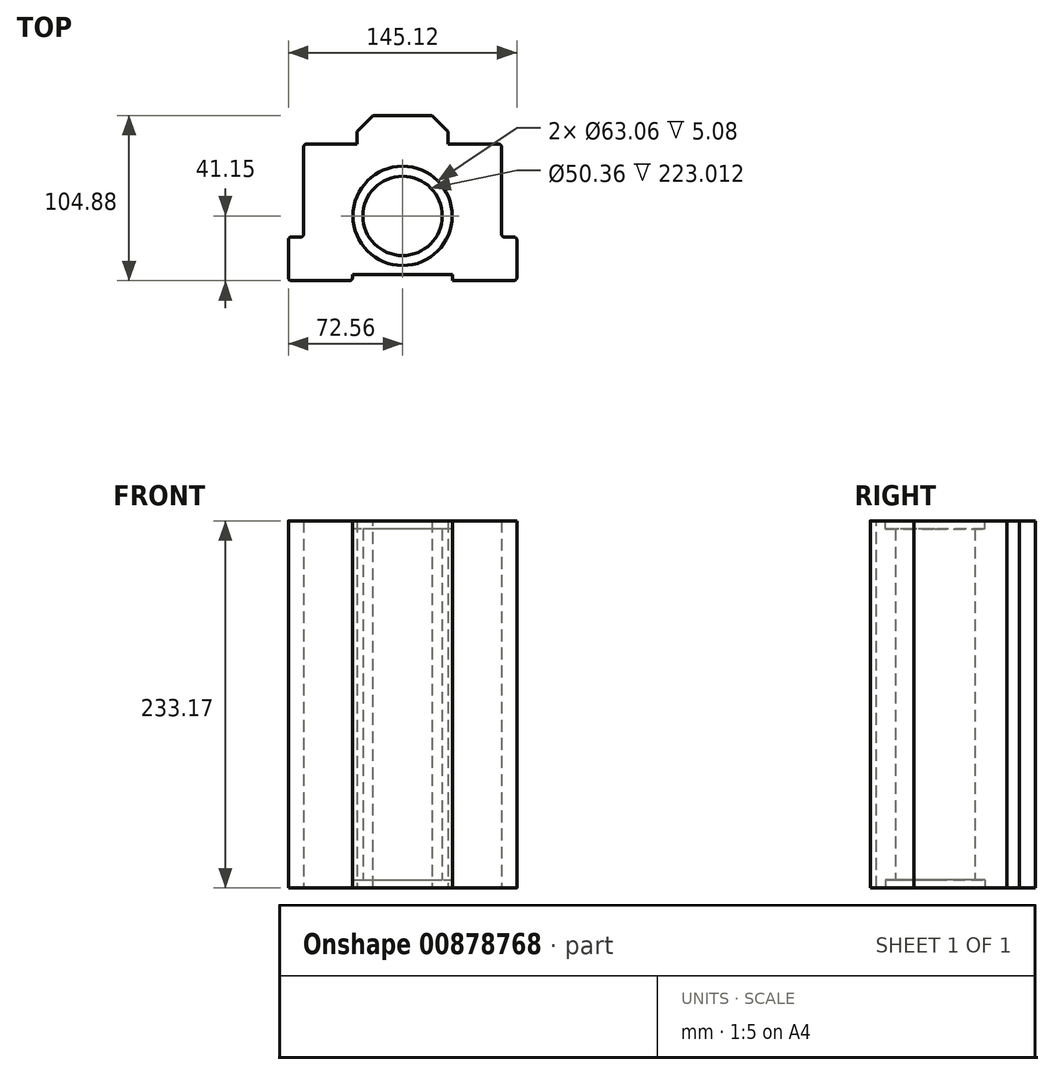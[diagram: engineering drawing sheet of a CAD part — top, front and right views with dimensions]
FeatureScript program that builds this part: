
annotation { "Feature Type Name" : "Feature", "Feature Type Description" : "" }
export const myFeature = defineFeature(function(context is Context, id is Id, definition is map)
    precondition{}
    {
        {
            var Q0;
            Q0=qCreatedBy(makeId("Top.planeOp"),FACE);
            var sketch = newSketch(context, id + "F0", { "sketchPlane" : qUnion([Q0])});
            skLineSegment(sketch, "E0.bottom", {"start": v(-62.86, 45.65) * mm, "end": v(-29, 45.65) * mm});
            skLineSegment(sketch, "E0.top", {"start": v(-62.86, -41.15) * mm, "end": v(62.86, -41.15) * mm});
            skLineSegment(sketch, "E0.left", {"start": v(-62.86, 45.65) * mm, "end": v(-62.86, -41.15) * mm});
            skLineSegment(sketch, "E0.right", {"start": v(62.86, 45.65) * mm, "end": v(62.86, -41.15) * mm});
            skCircle(sketch, "E1", {"center": v(0, 0) * mm, "radius": 25.18 * mm});
            skLineSegment(sketch, "E2.top", {"start": v(-29, 63.73) * mm, "end": v(29, 63.73) * mm});
            skLineSegment(sketch, "E2.left", {"start": v(-29, 45.65) * mm, "end": v(-29, 63.73) * mm});
            skLineSegment(sketch, "E2.right", {"start": v(29, 45.65) * mm, "end": v(29, 63.73) * mm});
            skLineSegment(sketch, "E3", {"start": v(0, 45.65) * mm, "end": v(0, -41.15) * mm, "construction": true});
            skLineSegment(sketch, "E4.trimOffspring", {"start": v(29, 45.65) * mm, "end": v(62.86, 45.65) * mm});
            skLineSegment(sketch, "E5", {"start": v(-29, 45.65) * mm, "end": v(0, 45.65) * mm});
            skLineSegment(sketch, "E6", {"start": v(29, 45.65) * mm, "end": v(0, 45.65) * mm});
            skLineSegment(sketch, "E7.bottom", {"start": v(-62.86, -41.15) * mm, "end": v(-72.56, -41.15) * mm});
            skLineSegment(sketch, "E7.top", {"start": v(-62.86, -13.43) * mm, "end": v(-72.56, -13.43) * mm});
            skLineSegment(sketch, "E7.left", {"start": v(-62.86, -41.15) * mm, "end": v(-62.86, -13.43) * mm});
            skLineSegment(sketch, "E7.right", {"start": v(-72.56, -41.15) * mm, "end": v(-72.56, -13.43) * mm});
            skLineSegment(sketch, "E8.bottom", {"start": v(62.86, -41.15) * mm, "end": v(72.56, -41.15) * mm});
            skLineSegment(sketch, "E8.top", {"start": v(62.86, -13.43) * mm, "end": v(72.56, -13.43) * mm});
            skLineSegment(sketch, "E8.left", {"start": v(62.86, -41.15) * mm, "end": v(62.86, -13.43) * mm});
            skLineSegment(sketch, "E8.right", {"start": v(72.56, -41.15) * mm, "end": v(72.56, -13.43) * mm});
            skSolve(sketch);
        }
        {
            var Q0;
            Q0 = qSketchRegion(id + "F0", true);
            extrude(context, id + "F1", {"entities" : qUnion([Q0]), "depth" : 233.17 * mm, "offsetDistance" : 25.4 * mm});
        }
        {
            var Q0;
            Q0=makeQuery(id+"F1.opExtrude","CAP_FACE",FACE,{"disambiguationData":[OSD([sQuery(id+"F0.wireOp",EDGE,"E0.bottom"),sQuery(id+"F0.wireOp",EDGE,"E0.top"),sQuery(id+"F0.wireOp",EDGE,"E0.left"),sQuery(id+"F0.wireOp",EDGE,"E0.right"),sQuery(id+"F0.wireOp",EDGE,"E1"),sQuery(id+"F0.wireOp",EDGE,"E2.top"),sQuery(id+"F0.wireOp",EDGE,"E2.left"),sQuery(id+"F0.wireOp",EDGE,"E2.right"),sQuery(id+"F0.wireOp",EDGE,"E4.trimOffspring"),sQuery(id+"F0.wireOp",EDGE,"E7.bottom"),sQuery(id+"F0.wireOp",EDGE,"E7.top"),sQuery(id+"F0.wireOp",EDGE,"E7.right"),sQuery(id+"F0.wireOp",EDGE,"E8.bottom"),sQuery(id+"F0.wireOp",EDGE,"E8.top"),sQuery(id+"F0.wireOp",EDGE,"E8.right")])],"isStart":false});
            var sketch = newSketch(context, id + "F2", { "sketchPlane" : qUnion([Q0])});
            skLineSegment(sketch, "E9.bottom", {"start": v(-31.8, -41.15) * mm, "end": v(31.8, -41.15) * mm});
            skLineSegment(sketch, "E9.top", {"start": v(-31.8, -37.14) * mm, "end": v(0, -37.14) * mm});
            skLineSegment(sketch, "E9.left", {"start": v(-31.8, -41.15) * mm, "end": v(-31.8, -37.14) * mm});
            skLineSegment(sketch, "E9.right", {"start": v(31.8, -41.15) * mm, "end": v(31.8, -37.14) * mm});
            skLineSegment(sketch, "E10", {"start": v(0, -41.15) * mm, "end": v(0, -37.14) * mm, "construction": true});
            skLineSegment(sketch, "E11", {"start": v(0, -37.14) * mm, "end": v(31.8, -37.14) * mm});
            skSolve(sketch);
        }
        {
            var Q0;
            Q0=makeQuery(id+"F2.imprint","IMPRINT",FACE,{"disambiguationData":[TD([[makeQuery(id+"F2.imprint","IMPRINT",EDGE,{"derivedFrom":sQuery(id+"F2.wireOp",EDGE,"E9.bottom")}),-1.0]])]});
            var Q1;
            Q1=makeQuery(id+"F1.opExtrude","CAP_FACE",FACE,{"disambiguationData":[OSD([sQuery(id+"F0.wireOp",EDGE,"E0.bottom"),sQuery(id+"F0.wireOp",EDGE,"E0.top"),sQuery(id+"F0.wireOp",EDGE,"E0.left"),sQuery(id+"F0.wireOp",EDGE,"E0.right"),sQuery(id+"F0.wireOp",EDGE,"E1"),sQuery(id+"F0.wireOp",EDGE,"E2.top"),sQuery(id+"F0.wireOp",EDGE,"E2.left"),sQuery(id+"F0.wireOp",EDGE,"E2.right"),sQuery(id+"F0.wireOp",EDGE,"E4.trimOffspring"),sQuery(id+"F0.wireOp",EDGE,"E7.bottom"),sQuery(id+"F0.wireOp",EDGE,"E7.top"),sQuery(id+"F0.wireOp",EDGE,"E7.right"),sQuery(id+"F0.wireOp",EDGE,"E8.bottom"),sQuery(id+"F0.wireOp",EDGE,"E8.top"),sQuery(id+"F0.wireOp",EDGE,"E8.right")])],"isStart":true});
            extrude(context, id + "F3", {"entities" : qUnion([Q0]), "operationType" : NewBodyOperationType.REMOVE, "endBound" : BoundingType.UP_TO_SURFACE, "oppositeDirection" : true, "depth" : 25.4 * mm, "endBoundEntityFace" : qUnion([Q1]), "offsetDistance" : 25.4 * mm});
        }
        {
            var Q0;
            Q0=makeQuery(id+"F1.opExtrude","SWEPT_EDGE",EDGE,{"disambiguationData":[OSD([sQuery(id+"F0.wireOp",EDGE,"E2.top"),sQuery(id+"F0.wireOp",EDGE,"E2.left")])]});
            var Q1;
            Q1=makeQuery(id+"F1.opExtrude","SWEPT_EDGE",EDGE,{"disambiguationData":[OSD([sQuery(id+"F0.wireOp",EDGE,"E2.top"),sQuery(id+"F0.wireOp",EDGE,"E2.right")])]});
            chamfer(context, id + "F4", {"entities" : qUnion([Q0, Q1]), "width" : 10.16 * mm, "tangentPropagation" : true});
        }
        {
            var Q0;
            Q0=makeQuery(id+"F1.opExtrude","SWEPT_EDGE",EDGE,{"disambiguationData":[OSD([sQuery(id+"F0.wireOp",EDGE,"E8.top"),sQuery(id+"F0.wireOp",EDGE,"E8.right")])]});
            var Q1;
            Q1=makeQuery(id+"F1.opExtrude","SWEPT_EDGE",EDGE,{"disambiguationData":[OSD([sQuery(id+"F0.wireOp",EDGE,"E8.bottom"),sQuery(id+"F0.wireOp",EDGE,"E8.right")])]});
            var Q2;
            Q2=makeQuery(id+"F3.boolean.opBoolean","COPY",EDGE,{"derivedFrom":makeQuery(id+"F3.opExtrude","SWEPT_EDGE",EDGE,{"disambiguationData":[OSD([sQuery(id+"F0.wireOp",EDGE,"E0.top"),sQuery(id+"F0.wireOp",EDGE,"E7.bottom"),sQuery(id+"F0.wireOp",EDGE,"E8.bottom"),sQuery(id+"F2.wireOp",EDGE,"E9.bottom"),sQuery(id+"F2.wireOp",EDGE,"E9.right")])]})});
            var Q3;
            Q3=makeQuery(id+"F3.boolean.opBoolean","COPY",EDGE,{"derivedFrom":makeQuery(id+"F3.opExtrude","SWEPT_EDGE",EDGE,{"disambiguationData":[OSD([sQuery(id+"F0.wireOp",EDGE,"E0.top"),sQuery(id+"F0.wireOp",EDGE,"E7.bottom"),sQuery(id+"F0.wireOp",EDGE,"E8.bottom"),sQuery(id+"F2.wireOp",EDGE,"E9.bottom"),sQuery(id+"F2.wireOp",EDGE,"E9.left")])]})});
            var Q4;
            Q4=makeQuery(id+"F1.opExtrude","SWEPT_EDGE",EDGE,{"disambiguationData":[OSD([sQuery(id+"F0.wireOp",EDGE,"E7.bottom"),sQuery(id+"F0.wireOp",EDGE,"E7.right")])]});
            var Q5;
            Q5=makeQuery(id+"F1.opExtrude","SWEPT_EDGE",EDGE,{"disambiguationData":[OSD([sQuery(id+"F0.wireOp",EDGE,"E7.top"),sQuery(id+"F0.wireOp",EDGE,"E7.right")])]});
            var Q6;
            Q6=makeQuery(id+"F1.opExtrude","SWEPT_EDGE",EDGE,{"disambiguationData":[OSD([sQuery(id+"F0.wireOp",EDGE,"E0.bottom"),sQuery(id+"F0.wireOp",EDGE,"E0.left")])]});
            var Q7;
            Q7=makeQuery(id+"F1.opExtrude","SWEPT_EDGE",EDGE,{"disambiguationData":[OSD([sQuery(id+"F0.wireOp",EDGE,"E0.right"),sQuery(id+"F0.wireOp",EDGE,"E4.trimOffspring")])]});
            var Q8;
            Q8=makeQuery(id+"F1.opExtrude","SWEPT_EDGE",EDGE,{"disambiguationData":[OSD([sQuery(id+"F0.wireOp",EDGE,"E0.right"),sQuery(id+"F0.wireOp",EDGE,"E8.top"),sQuery(id+"F0.wireOp",EDGE,"E8.left")])]});
            var Q9;
            Q9=makeQuery(id+"F1.opExtrude","SWEPT_EDGE",EDGE,{"disambiguationData":[OSD([sQuery(id+"F0.wireOp",EDGE,"E0.left"),sQuery(id+"F0.wireOp",EDGE,"E7.top"),sQuery(id+"F0.wireOp",EDGE,"E7.left")])]});
            fillet(context, id + "F5", {"entities" : qUnion([Q0, Q1, Q2, Q3, Q4, Q5, Q6, Q7, Q8, Q9]), "radius" : 2 * mm, "tangentPropagation" : true, "allowEdgeOverflow" : false});
        }
        {
            var Q0;
            Q0=makeQuery(id+"F1.opExtrude","CAP_FACE",FACE,{"disambiguationData":[OSD([sQuery(id+"F0.wireOp",EDGE,"E0.bottom"),sQuery(id+"F0.wireOp",EDGE,"E0.top"),sQuery(id+"F0.wireOp",EDGE,"E0.left"),sQuery(id+"F0.wireOp",EDGE,"E0.right"),sQuery(id+"F0.wireOp",EDGE,"E1"),sQuery(id+"F0.wireOp",EDGE,"E2.top"),sQuery(id+"F0.wireOp",EDGE,"E2.left"),sQuery(id+"F0.wireOp",EDGE,"E2.right"),sQuery(id+"F0.wireOp",EDGE,"E4.trimOffspring"),sQuery(id+"F0.wireOp",EDGE,"E7.bottom"),sQuery(id+"F0.wireOp",EDGE,"E7.top"),sQuery(id+"F0.wireOp",EDGE,"E7.right"),sQuery(id+"F0.wireOp",EDGE,"E8.bottom"),sQuery(id+"F0.wireOp",EDGE,"E8.top"),sQuery(id+"F0.wireOp",EDGE,"E8.right")])],"isStart":true});
            var sketch = newSketch(context, id + "F6", { "sketchPlane" : qUnion([Q0])});
            skCircle(sketch, "E12.0", {"center": v(0, 0) * mm, "radius": 31.53 * mm});
            skSolve(sketch);
        }
        {
            var Q0;
            Q0 = qSketchRegion(id + "F6", true);
            extrude(context, id + "F7", {"entities" : qUnion([Q0]), "operationType" : NewBodyOperationType.REMOVE, "oppositeDirection" : true, "depth" : 5.08 * mm, "offsetDistance" : 25.4 * mm});
        }
        {
            var Q0;
            Q0=makeQuery(id+"F1.opExtrude","CAP_FACE",FACE,{"disambiguationData":[OSD([sQuery(id+"F0.wireOp",EDGE,"E0.bottom"),sQuery(id+"F0.wireOp",EDGE,"E0.top"),sQuery(id+"F0.wireOp",EDGE,"E0.left"),sQuery(id+"F0.wireOp",EDGE,"E0.right"),sQuery(id+"F0.wireOp",EDGE,"E1"),sQuery(id+"F0.wireOp",EDGE,"E2.top"),sQuery(id+"F0.wireOp",EDGE,"E2.left"),sQuery(id+"F0.wireOp",EDGE,"E2.right"),sQuery(id+"F0.wireOp",EDGE,"E4.trimOffspring"),sQuery(id+"F0.wireOp",EDGE,"E7.bottom"),sQuery(id+"F0.wireOp",EDGE,"E7.top"),sQuery(id+"F0.wireOp",EDGE,"E7.right"),sQuery(id+"F0.wireOp",EDGE,"E8.bottom"),sQuery(id+"F0.wireOp",EDGE,"E8.top"),sQuery(id+"F0.wireOp",EDGE,"E8.right")])],"isStart":false});
            var sketch = newSketch(context, id + "F8", { "sketchPlane" : qUnion([Q0])});
            skCircle(sketch, "E13.0", {"center": v(0, 0) * mm, "radius": 31.53 * mm});
            skSolve(sketch);
        }
        {
            var Q0;
            Q0 = qSketchRegion(id + "F8", true);
            extrude(context, id + "F9", {"entities" : qUnion([Q0]), "operationType" : NewBodyOperationType.REMOVE, "oppositeDirection" : true, "depth" : 5.08 * mm, "offsetDistance" : 25.4 * mm});
        }
    });
